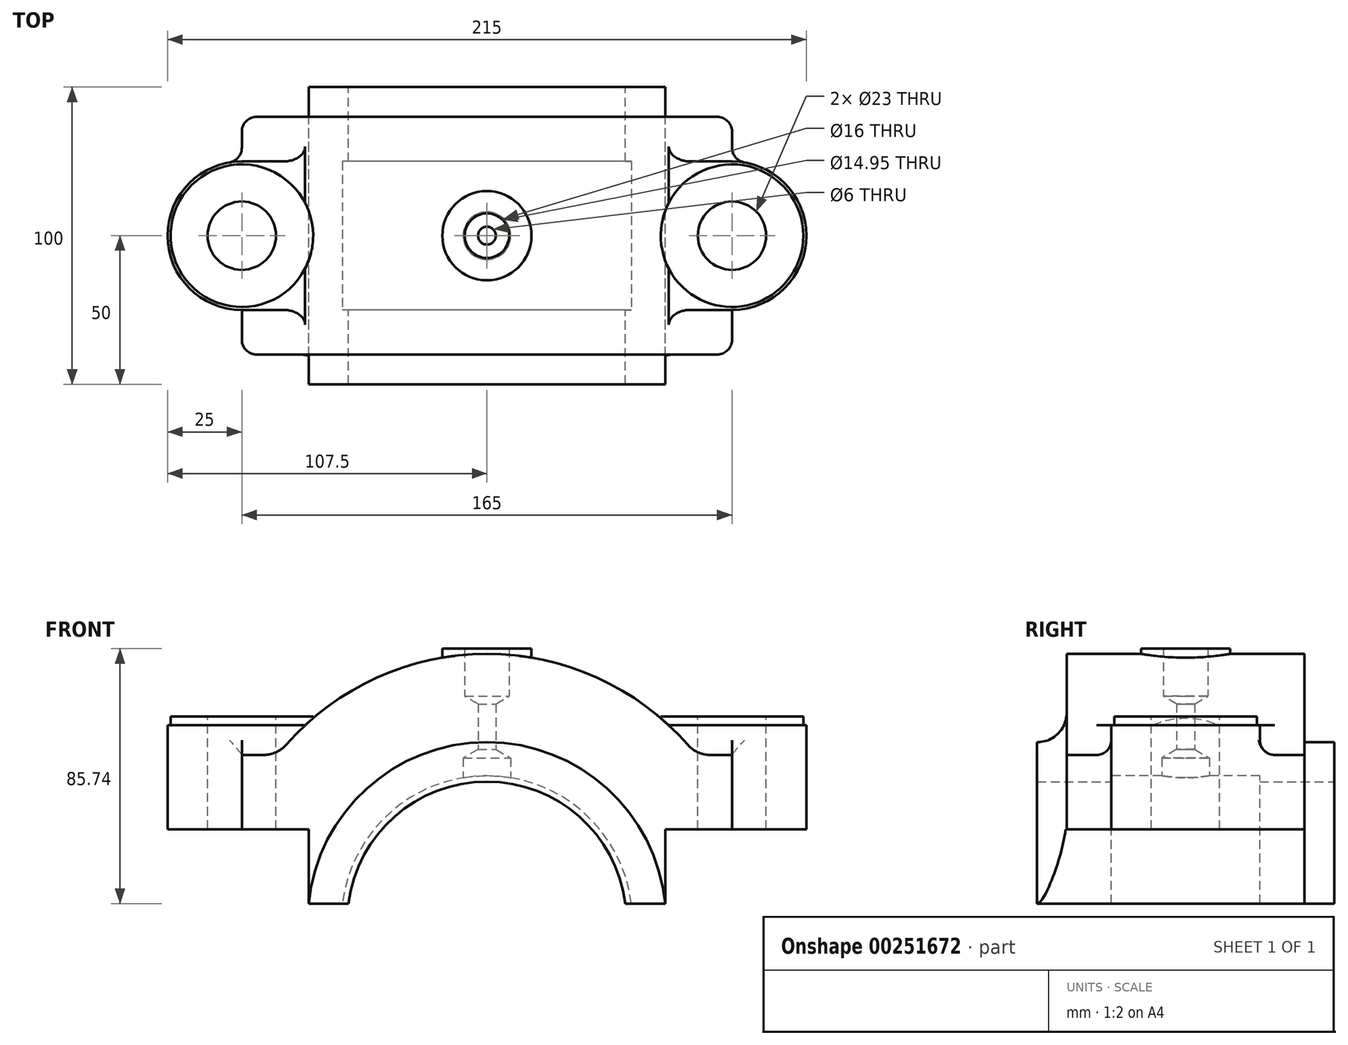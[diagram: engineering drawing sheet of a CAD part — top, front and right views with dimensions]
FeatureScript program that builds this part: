
annotation { "Feature Type Name" : "Feature", "Feature Type Description" : "" }
export const myFeature = defineFeature(function(context is Context, id is Id, definition is map)
    precondition{}
    {
        {
            var Q0;
            Q0=qCreatedBy(makeId("Front.planeOp"),FACE);
            var sketch = newSketch(context, id + "F0", { "sketchPlane" : qUnion([Q0])});
            skLineSegment(sketch, "E0", {"start": v(-60, 6) * mm, "end": v(-60, 31) * mm});
            skLineSegment(sketch, "E1", {"start": v(-60, 31) * mm, "end": v(-82.5, 31) * mm});
            skLineSegment(sketch, "E2", {"start": v(-82.5, 31) * mm, "end": v(-82.5, 56) * mm});
            skLineSegment(sketch, "E3", {"start": v(-82.5, 56) * mm, "end": v(-70.46, 56) * mm});
            skArc(sketch, "E4.0", {"start": v(-60, 6) * mm, "mid": v(0, 60.3) * mm, "end": v(60, 6) * mm});
            skArc(sketch, "E5", {"start": v(-70.46, 56) * mm, "mid": v(0, 90) * mm, "end": v(70.46, 56) * mm});
            skLineSegment(sketch, "E6.MirrorCS", {"start": v(60, 31) * mm, "end": v(82.5, 31) * mm});
            skLineSegment(sketch, "E7.MirrorCS", {"start": v(82.5, 56) * mm, "end": v(70.46, 56) * mm});
            skLineSegment(sketch, "E8.MirrorCS", {"start": v(60, 6) * mm, "end": v(60, 31) * mm});
            skLineSegment(sketch, "E9.MirrorCS", {"start": v(82.5, 31) * mm, "end": v(82.5, 56) * mm});
            skSolve(sketch);
        }
        {
            var Q0;
            Q0 = qSketchRegion(id + "F0", true);
            extrude(context, id + "F1", {"entities" : qUnion([Q0]), "depth" : 40 * mm, "hasSecondDirection" : true, "secondDirectionOppositeDirection" : true, "secondDirectionDepth" : 40 * mm});
        }
        {
            var Q0;
            Q0=qCreatedBy(makeId("Front.planeOp"),FACE);
            var sketch = newSketch(context, id + "F2", { "sketchPlane" : qUnion([Q0])});
            skArc(sketch, "E10", {"start": v(-46.62, 6) * mm, "mid": v(0, 47) * mm, "end": v(46.62, 6) * mm});
            skArc(sketch, "E11", {"start": v(-60, 6) * mm, "mid": v(0, 60.3) * mm, "end": v(60, 6) * mm});
            skLineSegment(sketch, "E12", {"start": v(-60, 6) * mm, "end": v(-46.62, 6) * mm});
            skLineSegment(sketch, "E13", {"start": v(46.62, 6) * mm, "end": v(60, 6) * mm});
            skSolve(sketch);
        }
        {
            var Q0;
            Q0 = qSketchRegion(id + "F2", true);
            extrude(context, id + "F3", {"entities" : qUnion([Q0]), "operationType" : NewBodyOperationType.ADD, "depth" : 50 * mm, "hasSecondDirection" : true, "secondDirectionOppositeDirection" : true, "secondDirectionDepth" : 50 * mm});
        }
        {
            var Q0;
            Q0=qCreatedBy(makeId("Front.planeOp"),FACE);
            var sketch = newSketch(context, id + "F4", { "sketchPlane" : qUnion([Q0])});
            skArc(sketch, "E14", {"start": v(46.62, 6) * mm, "mid": v(0, 47) * mm, "end": v(-46.62, 6) * mm});
            skArc(sketch, "E15", {"start": v(48.63, 6) * mm, "mid": v(0, 49) * mm, "end": v(-48.63, 6) * mm});
            skLineSegment(sketch, "E16", {"start": v(-46.62, 6) * mm, "end": v(-48.63, 6) * mm});
            skLineSegment(sketch, "E17", {"start": v(46.62, 6) * mm, "end": v(48.63, 6) * mm});
            skSolve(sketch);
        }
        {
            var Q0;
            Q0 = qSketchRegion(id + "F4", true);
            extrude(context, id + "F5", {"entities" : qUnion([Q0]), "operationType" : NewBodyOperationType.REMOVE, "oppositeDirection" : true, "depth" : 25 * mm, "hasSecondDirection" : true, "secondDirectionOppositeDirection" : false, "secondDirectionDepth" : 25 * mm});
        }
        {
            var Q0;
            Q0=qCreatedBy(makeId("Top.planeOp"),FACE);
            cPlane(context, id + "F6", {"entities" : qUnion([Q0]), "cplaneType" : CPlaneType.OFFSET, "offset" : 31 * mm, "width" : 150 * mm, "height" : 150 * mm});
        }
        {
            var Q0;
            Q0=qCreatedBy(id+"F6.planeOp",FACE);
            var sketch = newSketch(context, id + "F7", { "sketchPlane" : qUnion([Q0])});
            skArc(sketch, "E18", {"start": v(-82.5, 25) * mm, "mid": v(-107.5, 0) * mm, "end": v(-82.5, -25) * mm});
            skLineSegment(sketch, "E19", {"start": v(-82.5, 25) * mm, "end": v(-50, 25) * mm});
            skLineSegment(sketch, "E20.MirrorCS", {"start": v(-82.5, -25) * mm, "end": v(-50, -25) * mm});
            skLineSegment(sketch, "E21", {"start": v(-50, 25) * mm, "end": v(-50, -25) * mm});
            skLineSegment(sketch, "E22.MirrorCS", {"start": v(82.5, 25) * mm, "end": v(50, 25) * mm});
            skArc(sketch, "E23.MirrorCS", {"start": v(82.5, 25) * mm, "mid": v(107.5, 0) * mm, "end": v(82.5, -25) * mm});
            skLineSegment(sketch, "E24.MirrorCS", {"start": v(82.5, -25) * mm, "end": v(50, -25) * mm});
            skLineSegment(sketch, "E25.MirrorCS", {"start": v(50, 25) * mm, "end": v(50, -25) * mm});
            skSolve(sketch);
        }
        {
            var Q0;
            Q0 = qSketchRegion(id + "F7", true);
            extrude(context, id + "F8", {"entities" : qUnion([Q0]), "operationType" : NewBodyOperationType.ADD, "depth" : 35 * mm});
        }
        {
            var Q0;
            Q0=makeQuery(id+"F8.opExtrude","CAP_FACE",FACE,{"disambiguationData":[OSD([sQuery(id+"F7.wireOp",EDGE,"E18"),sQuery(id+"F7.wireOp",EDGE,"E19"),sQuery(id+"F7.wireOp",EDGE,"E20.MirrorCS"),sQuery(id+"F7.wireOp",EDGE,"E21")])],"isStart":false});
            var sketch = newSketch(context, id + "F9", { "sketchPlane" : qUnion([Q0])});
            skCircle(sketch, "E26", {"center": v(-82.5, 0) * mm, "radius": 24 * mm});
            skCircle(sketch, "E27.MirrorC", {"center": v(82.5, 0) * mm, "radius": 24 * mm});
            skSolve(sketch);
        }
        {
            var Q0;
            Q0 = qSketchRegion(id + "F9", true);
            extrude(context, id + "F10", {"entities" : qUnion([Q0]), "operationType" : NewBodyOperationType.ADD, "depth" : 3 * mm});
        }
        {
            var Q0;
            Q0=qCreatedBy(makeId("Front.planeOp"),FACE);
            var sketch = newSketch(context, id + "F11", { "sketchPlane" : qUnion([Q0])});
            skLineSegment(sketch, "E28", {"start": v(0, 84.74) * mm, "end": v(15, 84.74) * mm});
            skLineSegment(sketch, "E29", {"start": v(15, 84.74) * mm, "end": v(15, 91.74) * mm});
            skLineSegment(sketch, "E30", {"start": v(15, 91.74) * mm, "end": v(0, 91.74) * mm});
            skLineSegment(sketch, "E31", {"start": v(0, 91.74) * mm, "end": v(0, 84.74) * mm});
            skLineSegment(sketch, "E32", {"start": v(0, 123.5) * mm, "end": v(0, 76.6) * mm, "construction": true});
            skArc(sketch, "E33", {"start": v(-61.14, 66.05) * mm, "mid": v(3.53, 89.93) * mm, "end": v(66.12, 61.06) * mm});
            skPoint(sketch, "E34", {"position": v(15, 88.74) * mm});
            skSolve(sketch);
        }
        {
            var Q0;
            Q0 = qSketchRegion(id + "F11", true);
            var Q1;
            Q1=sQuery(id+"F11.wireOp",EDGE,"E32");
            revolve(context, id + "F12", {"operationType" : NewBodyOperationType.ADD, "entities" : qUnion([Q0]), "axis" : qUnion([Q1]), "revolveType" : RevolveType.FULL});
        }
        {
            var Q0;
            Q0=makeQuery(id+"F10.opExtrude","CAP_FACE",FACE,{"disambiguationData":[OSD([sQuery(id+"F9.wireOp",EDGE,"E26")])],"isStart":false});
            var sketch = newSketch(context, id + "F13", { "sketchPlane" : qUnion([Q0])});
            skPoint(sketch, "E35", {"position": v(-82.5, 0) * mm});
            skPoint(sketch, "E36.MirrorP", {"position": v(82.5, 0) * mm});
            skSolve(sketch);
        }
        {
            var Q0;
            Q0=sQuery(id+"F13.wireOp",VERTEX,"E36.MirrorP");
            var Q1;
            Q1=sQuery(id+"F13.wireOp",VERTEX,"E35");
            var Q2;
            Q2=makeQuery(id+"F1.opExtrude","SWEPT_BODY",BODY,{"disambiguationData":[OSD([sQuery(id+"F0.wireOp",EDGE,"E0"),sQuery(id+"F0.wireOp",EDGE,"E1"),sQuery(id+"F0.wireOp",EDGE,"E2"),sQuery(id+"F0.wireOp",EDGE,"E3"),sQuery(id+"F0.wireOp",EDGE,"E4.0"),sQuery(id+"F0.wireOp",EDGE,"E5"),sQuery(id+"F0.wireOp",EDGE,"E6.MirrorCS"),sQuery(id+"F0.wireOp",EDGE,"E7.MirrorCS"),sQuery(id+"F0.wireOp",EDGE,"E8.MirrorCS"),sQuery(id+"F0.wireOp",EDGE,"E9.MirrorCS")])]});
            hole(context, id + "F14", {"style" : HoleStyle.SIMPLE, "endStyle" : HoleEndStyle.THROUGH, "holeDiameter" : 23 * mm, "tappedDepth" : 12 * mm, "tapClearance" : 3, "locations" : qUnion([Q0, Q1]), "scope" : qUnion([Q2])});
        }
        {
            var Q0;
            Q0=qCreatedBy(makeId("Front.planeOp"),FACE);
            var sketch = newSketch(context, id + "F15", { "sketchPlane" : qUnion([Q0])});
            skLineSegment(sketch, "E37", {"start": v(8, 44) * mm, "end": v(8, 55) * mm});
            skLineSegment(sketch, "E38", {"start": v(8, 55) * mm, "end": v(3, 57.89) * mm});
            skLineSegment(sketch, "E39", {"start": v(3, 57.89) * mm, "end": v(3, 73.16) * mm});
            skLineSegment(sketch, "E40", {"start": v(3, 73.16) * mm, "end": v(7.48, 75.74) * mm});
            skLineSegment(sketch, "E41", {"start": v(7.48, 75.74) * mm, "end": v(7.48, 95.74) * mm});
            skLineSegment(sketch, "E42", {"start": v(7.48, 95.74) * mm, "end": v(0, 95.74) * mm});
            skLineSegment(sketch, "E43", {"start": v(0, 95.74) * mm, "end": v(0, 44) * mm});
            skLineSegment(sketch, "E44", {"start": v(0, 44) * mm, "end": v(8, 44) * mm});
            skLineSegment(sketch, "E45", {"start": v(0, 105.41) * mm, "end": v(0, 38.08) * mm, "construction": true});
            skArc(sketch, "E46.0", {"start": v(-46.62, 6) * mm, "mid": v(0, 47) * mm, "end": v(46.62, 6) * mm, "construction": true});
            skPoint(sketch, "E47", {"position": v(0, 47) * mm});
            skSolve(sketch);
        }
        {
            var Q0;
            Q0=makeQuery(id+"F15.imprint","IMPRINT",FACE,{"disambiguationData":[TD([[makeQuery(id+"F15.imprint","IMPRINT",EDGE,{"derivedFrom":sQuery(id+"F15.wireOp",EDGE,"E37")}),1.0]])]});
            var Q1;
            Q1=sQuery(id+"F15.wireOp",EDGE,"E45");
            revolve(context, id + "F16", {"operationType" : NewBodyOperationType.REMOVE, "entities" : qUnion([Q0]), "axis" : qUnion([Q1]), "revolveType" : RevolveType.FULL, "oppositeDirection" : true});
        }
        {
            var Q0;
            Q0=makeQuery(id+"F1.opExtrude","CAP_EDGE",EDGE,{"disambiguationData":[OSD([sQuery(id+"F0.wireOp",EDGE,"E2")])],"isStart":true});
            var Q1;
            Q1=makeQuery(id+"F1.opExtrude","CAP_EDGE",EDGE,{"disambiguationData":[OSD([sQuery(id+"F0.wireOp",EDGE,"E9.MirrorCS")])],"isStart":false});
            var Q2;
            Q2=makeQuery(id+"F1.opExtrude","CAP_EDGE",EDGE,{"disambiguationData":[OSD([sQuery(id+"F0.wireOp",EDGE,"E2")])],"isStart":false});
            var Q3;
            Q3=makeQuery(id+"F1.opExtrude","CAP_EDGE",EDGE,{"disambiguationData":[OSD([sQuery(id+"F0.wireOp",EDGE,"E9.MirrorCS")])],"isStart":true});
            fillet(context, id + "F17", {"entities" : qUnion([Q0, Q1, Q2, Q3]), "radius" : 5 * mm, "tangentPropagation" : true, "allowEdgeOverflow" : false});
        }
        {
            var Q0;
            {var subQ0=sQuery(id+"F7.wireOp",EDGE,"E24.MirrorCS");var subQ1=sQuery(id+"F7.wireOp",EDGE,"E23.MirrorCS");Q0=makeQuery(id+"F8.boolean.opBoolean","SPLIT",EDGE,{"disambiguationData":[TD([makeQuery(id+"F1.opExtrude","SWEPT_FACE",FACE,{"disambiguationData":[OSD([sQuery(id+"F0.wireOp",EDGE,"E6.MirrorCS")])]})])],"derivedFrom":makeQuery(id+"F8.opExtrude","SWEPT_EDGE",EDGE,{"disambiguationData":[OSD([subQ1,subQ0])]})});}
            var Q1;
            {var subQ0=sQuery(id+"F7.wireOp",EDGE,"E18");var subQ1=sQuery(id+"F7.wireOp",EDGE,"E20.MirrorCS");Q1=makeQuery(id+"F8.boolean.opBoolean","SPLIT",EDGE,{"disambiguationData":[TD([makeQuery(id+"F1.opExtrude","SWEPT_FACE",FACE,{"disambiguationData":[OSD([sQuery(id+"F0.wireOp",EDGE,"E1")])]})])],"derivedFrom":makeQuery(id+"F8.opExtrude","SWEPT_EDGE",EDGE,{"disambiguationData":[OSD([subQ0,subQ1])]})});}
            var Q2;
            {var subQ0=sQuery(id+"F7.wireOp",EDGE,"E18");var subQ1=sQuery(id+"F7.wireOp",EDGE,"E19");Q2=makeQuery(id+"F8.boolean.opBoolean","SPLIT",EDGE,{"disambiguationData":[TD([makeQuery(id+"F1.opExtrude","SWEPT_FACE",FACE,{"disambiguationData":[OSD([sQuery(id+"F0.wireOp",EDGE,"E1")])]})])],"derivedFrom":makeQuery(id+"F8.opExtrude","SWEPT_EDGE",EDGE,{"disambiguationData":[OSD([subQ0,subQ1])]})});}
            var Q3;
            {var subQ0=sQuery(id+"F7.wireOp",EDGE,"E22.MirrorCS");var subQ1=sQuery(id+"F7.wireOp",EDGE,"E23.MirrorCS");Q3=makeQuery(id+"F8.boolean.opBoolean","SPLIT",EDGE,{"disambiguationData":[TD([makeQuery(id+"F1.opExtrude","SWEPT_FACE",FACE,{"disambiguationData":[OSD([sQuery(id+"F0.wireOp",EDGE,"E6.MirrorCS")])]})])],"derivedFrom":makeQuery(id+"F8.opExtrude","SWEPT_EDGE",EDGE,{"disambiguationData":[OSD([subQ0,subQ1])]})});}
            fillet(context, id + "F18", {"entities" : qUnion([Q0, Q1, Q2, Q3]), "radius" : 5 * mm, "tangentPropagation" : true, "allowEdgeOverflow" : false});
        }
        {
            var Q0;
            {var subQ0=sQuery(id+"F0.wireOp",EDGE,"E5");var subQ1=sQuery(id+"F0.wireOp",EDGE,"E3");Q0=makeQuery(id+"F8.boolean.opBoolean","SPLIT",EDGE,{"disambiguationData":[TD([makeQuery(id+"F8.opExtrude","SWEPT_FACE",FACE,{"disambiguationData":[OSD([sQuery(id+"F7.wireOp",EDGE,"E19")])]})])],"derivedFrom":makeQuery(id+"F1.opExtrude","SWEPT_EDGE",EDGE,{"disambiguationData":[OSD([subQ1,subQ0])]})});}
            var Q1;
            {var subQ0=sQuery(id+"F0.wireOp",EDGE,"E5");var subQ1=sQuery(id+"F0.wireOp",EDGE,"E3");Q1=makeQuery(id+"F8.boolean.opBoolean","SPLIT",EDGE,{"disambiguationData":[TD([makeQuery(id+"F8.opExtrude","SWEPT_FACE",FACE,{"disambiguationData":[OSD([sQuery(id+"F7.wireOp",EDGE,"E20.MirrorCS")])]})])],"derivedFrom":makeQuery(id+"F1.opExtrude","SWEPT_EDGE",EDGE,{"disambiguationData":[OSD([subQ1,subQ0])]})});}
            var Q2;
            {var subQ0=sQuery(id+"F0.wireOp",EDGE,"E7.MirrorCS");var subQ1=sQuery(id+"F0.wireOp",EDGE,"E5");Q2=makeQuery(id+"F8.boolean.opBoolean","SPLIT",EDGE,{"disambiguationData":[TD([makeQuery(id+"F8.opExtrude","SWEPT_FACE",FACE,{"disambiguationData":[OSD([sQuery(id+"F7.wireOp",EDGE,"E22.MirrorCS")])]})])],"derivedFrom":makeQuery(id+"F1.opExtrude","SWEPT_EDGE",EDGE,{"disambiguationData":[OSD([subQ1,subQ0])]})});}
            var Q3;
            {var subQ0=sQuery(id+"F0.wireOp",EDGE,"E7.MirrorCS");var subQ1=sQuery(id+"F0.wireOp",EDGE,"E5");Q3=makeQuery(id+"F8.boolean.opBoolean","SPLIT",EDGE,{"disambiguationData":[TD([makeQuery(id+"F8.opExtrude","SWEPT_FACE",FACE,{"disambiguationData":[OSD([sQuery(id+"F7.wireOp",EDGE,"E24.MirrorCS")])]})])],"derivedFrom":makeQuery(id+"F1.opExtrude","SWEPT_EDGE",EDGE,{"disambiguationData":[OSD([subQ1,subQ0])]})});}
            fillet(context, id + "F19", {"entities" : qUnion([Q0, Q1, Q2, Q3]), "radius" : 10 * mm, "tangentPropagation" : true, "allowEdgeOverflow" : false});
        }
        {
            var Q0;
            Q0=makeQuery(id+"F1.opExtrude","CAP_EDGE",EDGE,{"disambiguationData":[OSD([sQuery(id+"F0.wireOp",EDGE,"E4.0")])],"isStart":true});
            var Q1;
            Q1=makeQuery(id+"F1.opExtrude","CAP_EDGE",EDGE,{"disambiguationData":[OSD([sQuery(id+"F0.wireOp",EDGE,"E4.0")])],"isStart":false});
            fillet(context, id + "F20", {"entities" : qUnion([Q0, Q1]), "radius" : 10 * mm, "tangentPropagation" : true, "allowEdgeOverflow" : false});
        }
        {
            var Q0;
            {var subQ0=makeQuery(id+"F8.opExtrude","SWEPT_FACE",FACE,{"disambiguationData":[OSD([sQuery(id+"F7.wireOp",EDGE,"E24.MirrorCS")])]});var subQ1=sQuery(id+"F0.wireOp",EDGE,"E7.MirrorCS");var subQ2=sQuery(id+"F0.wireOp",EDGE,"E5");Q0=makeQuery(id+"F19.opFillet","BLEND_EDGE",EDGE,{"blendedFrom":[makeQuery(id+"F8.boolean.opBoolean","SPLIT",EDGE,{"disambiguationData":[TD([subQ0])],"derivedFrom":makeQuery(id+"F1.opExtrude","SWEPT_EDGE",EDGE,{"disambiguationData":[OSD([subQ2,subQ1])]})}),subQ0],"blendedInto":[subQ0]});}
            var Q1;
            {var subQ0=makeQuery(id+"F8.opExtrude","SWEPT_FACE",FACE,{"disambiguationData":[OSD([sQuery(id+"F7.wireOp",EDGE,"E22.MirrorCS")])]});var subQ1=sQuery(id+"F0.wireOp",EDGE,"E7.MirrorCS");var subQ2=sQuery(id+"F0.wireOp",EDGE,"E5");Q1=makeQuery(id+"F19.opFillet","BLEND_EDGE",EDGE,{"blendedFrom":[makeQuery(id+"F8.boolean.opBoolean","SPLIT",EDGE,{"disambiguationData":[TD([subQ0])],"derivedFrom":makeQuery(id+"F1.opExtrude","SWEPT_EDGE",EDGE,{"disambiguationData":[OSD([subQ2,subQ1])]})}),subQ0],"blendedInto":[subQ0]});}
            var Q2;
            {var subQ0=makeQuery(id+"F8.opExtrude","SWEPT_FACE",FACE,{"disambiguationData":[OSD([sQuery(id+"F7.wireOp",EDGE,"E20.MirrorCS")])]});var subQ1=sQuery(id+"F0.wireOp",EDGE,"E5");var subQ2=sQuery(id+"F0.wireOp",EDGE,"E3");Q2=makeQuery(id+"F19.opFillet","BLEND_EDGE",EDGE,{"blendedFrom":[makeQuery(id+"F8.boolean.opBoolean","SPLIT",EDGE,{"disambiguationData":[TD([subQ0])],"derivedFrom":makeQuery(id+"F1.opExtrude","SWEPT_EDGE",EDGE,{"disambiguationData":[OSD([subQ2,subQ1])]})}),subQ0],"blendedInto":[subQ0]});}
            var Q3;
            {var subQ0=makeQuery(id+"F8.opExtrude","SWEPT_FACE",FACE,{"disambiguationData":[OSD([sQuery(id+"F7.wireOp",EDGE,"E19")])]});var subQ1=sQuery(id+"F0.wireOp",EDGE,"E5");var subQ2=sQuery(id+"F0.wireOp",EDGE,"E3");Q3=makeQuery(id+"F19.opFillet","BLEND_EDGE",EDGE,{"blendedFrom":[makeQuery(id+"F8.boolean.opBoolean","SPLIT",EDGE,{"disambiguationData":[TD([subQ0])],"derivedFrom":makeQuery(id+"F1.opExtrude","SWEPT_EDGE",EDGE,{"disambiguationData":[OSD([subQ2,subQ1])]})}),subQ0],"blendedInto":[subQ0]});}
            fillet(context, id + "F21", {"entities" : qUnion([Q0, Q1, Q2, Q3]), "radius" : 5 * mm, "tangentPropagation" : true, "allowEdgeOverflow" : false});
        }
    });
